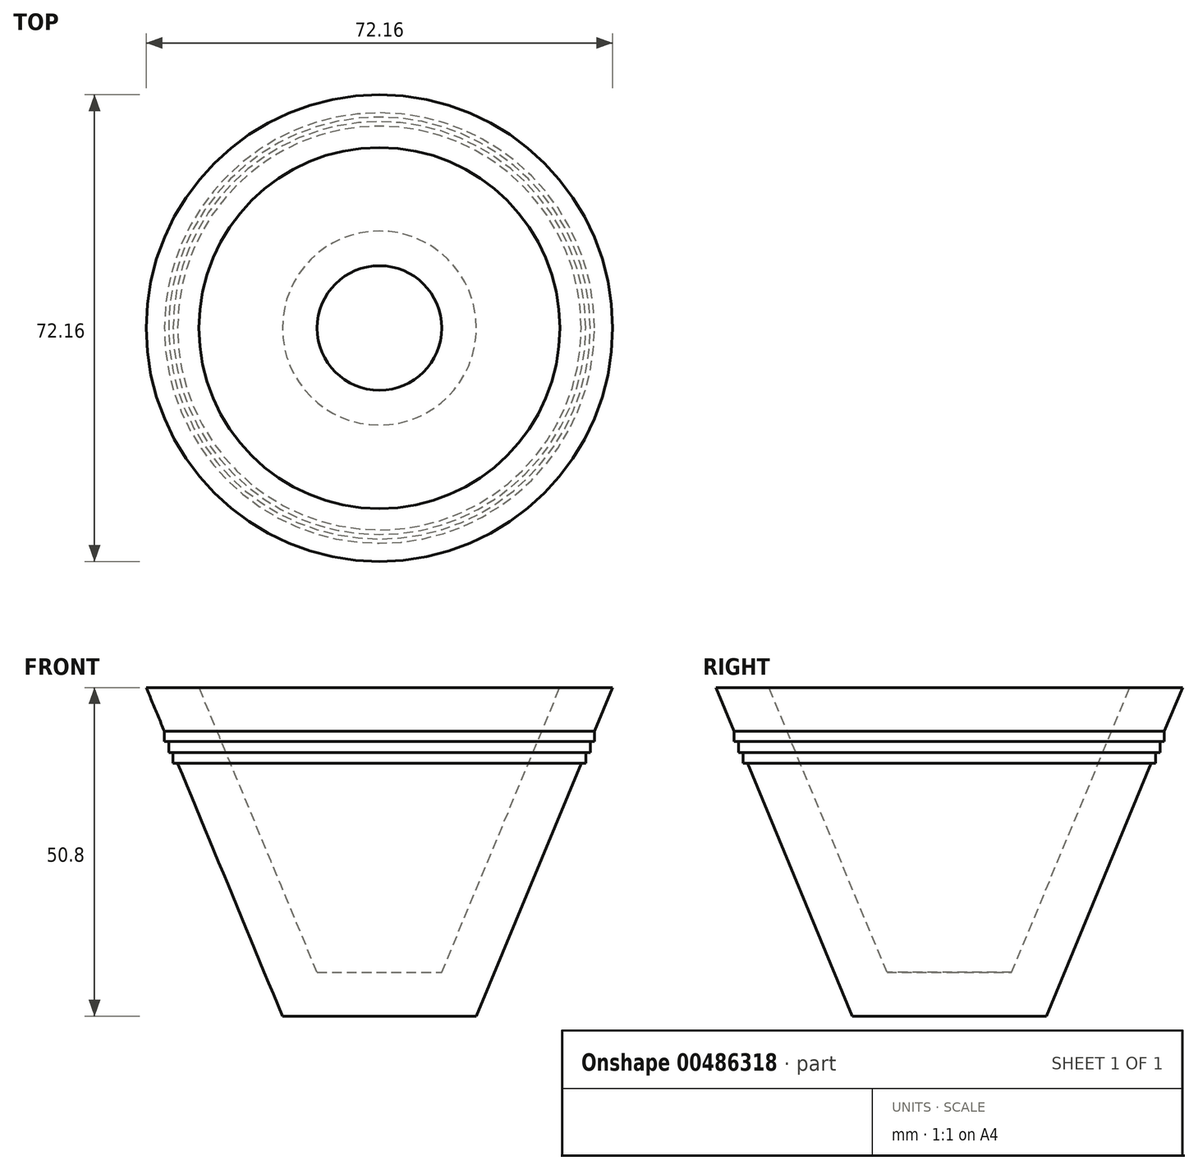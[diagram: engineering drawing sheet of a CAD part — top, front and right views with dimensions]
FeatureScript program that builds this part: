
annotation { "Feature Type Name" : "Feature", "Feature Type Description" : "" }
export const myFeature = defineFeature(function(context is Context, id is Id, definition is map)
    precondition{}
    {
        {
            var Q0;
            Q0=qCreatedBy(makeId("Front.planeOp"),FACE);
            var sketch = newSketch(context, id + "F0", { "sketchPlane" : qUnion([Q0])});
            skLineSegment(sketch, "E0", {"start": v(0, 0) * mm, "end": v(0, 50.8) * mm});
            skLineSegment(sketch, "E1", {"start": v(0, 0) * mm, "end": v(15, 0) * mm});
            skLineSegment(sketch, "E2", {"start": v(15, 0) * mm, "end": v(36.08, 50.8) * mm});
            skLineSegment(sketch, "E3", {"start": v(36.08, 50.8) * mm, "end": v(27.92, 50.8) * mm});
            skLineSegment(sketch, "E4", {"start": v(27.92, 50.8) * mm, "end": v(9.64, 6.74) * mm});
            skLineSegment(sketch, "E5", {"start": v(9.64, 6.74) * mm, "end": v(0, 6.74) * mm});
            skLineSegment(sketch, "E6", {"start": v(33.27, 44.03) * mm, "end": v(33.27, 42.44) * mm});
            skLineSegment(sketch, "E7", {"start": v(33.27, 42.44) * mm, "end": v(32.61, 42.44) * mm});
            skLineSegment(sketch, "E8", {"start": v(32.61, 42.44) * mm, "end": v(32.61, 40.77) * mm});
            skLineSegment(sketch, "E9", {"start": v(32.61, 40.77) * mm, "end": v(31.92, 40.77) * mm});
            skLineSegment(sketch, "E10", {"start": v(31.92, 40.77) * mm, "end": v(31.92, 39.08) * mm});
            skLineSegment(sketch, "E11", {"start": v(31.92, 39.08) * mm, "end": v(31.22, 39.08) * mm});
            skSolve(sketch);
        }
        {
            var Q0;
            Q0 = qSketchRegion(id + "F0", true);
            var Q1;
            Q1=sQuery(id+"F0.wireOp",EDGE,"E0");
            revolve(context, id + "F1", {"entities" : qUnion([Q0]), "axis" : qUnion([Q1]), "revolveType" : RevolveType.FULL});
        }
    });
